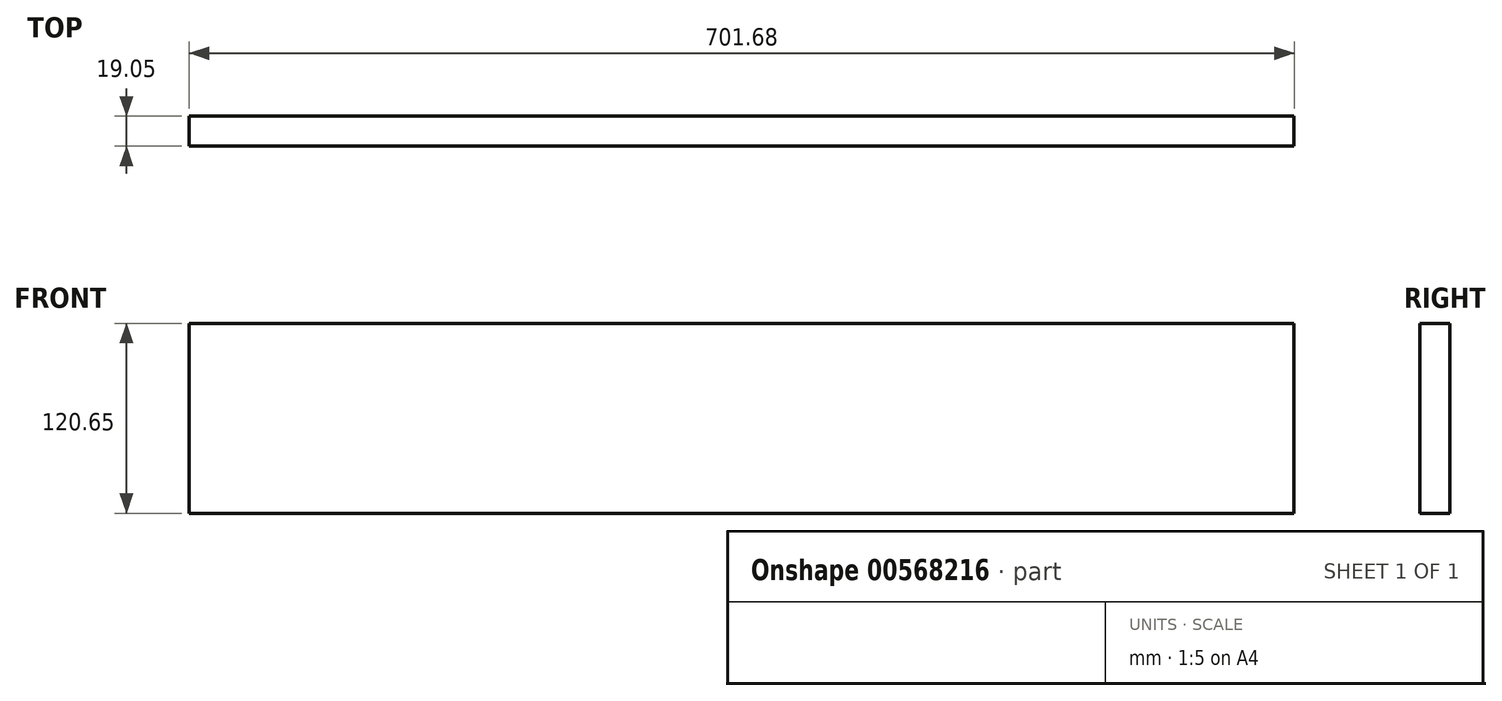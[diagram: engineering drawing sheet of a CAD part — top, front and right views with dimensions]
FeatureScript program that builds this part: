
annotation { "Feature Type Name" : "Feature", "Feature Type Description" : "" }
export const myFeature = defineFeature(function(context is Context, id is Id, definition is map)
    precondition{}
    {
        {
            var Q0;
            Q0=qCreatedBy(makeId("Front.planeOp"),FACE);
            var sketch = newSketch(context, id + "F0", { "sketchPlane" : qUnion([Q0])});
            skLineSegment(sketch, "E0.bottom", {"start": v(0, 0) * mm, "end": v(701.68, 0) * mm});
            skLineSegment(sketch, "E0.top", {"start": v(0, 120.65) * mm, "end": v(701.68, 120.65) * mm});
            skLineSegment(sketch, "E0.left", {"start": v(0, 0) * mm, "end": v(0, 120.65) * mm});
            skLineSegment(sketch, "E0.right", {"start": v(701.68, 0) * mm, "end": v(701.68, 120.65) * mm});
            skSolve(sketch);
        }
        {
            var Q0;
            Q0=makeQuery(id+"F0.imprint","IMPRINT",FACE,{"disambiguationData":[TD([[makeQuery(id+"F0.imprint","IMPRINT",EDGE,{"derivedFrom":sQuery(id+"F0.wireOp",EDGE,"E0.bottom")}),1.0]])]});
            extrude(context, id + "F1", {"entities" : qUnion([Q0]), "depth" : 19.05 * mm, "offsetDistance" : 25.4 * mm});
        }
    });
